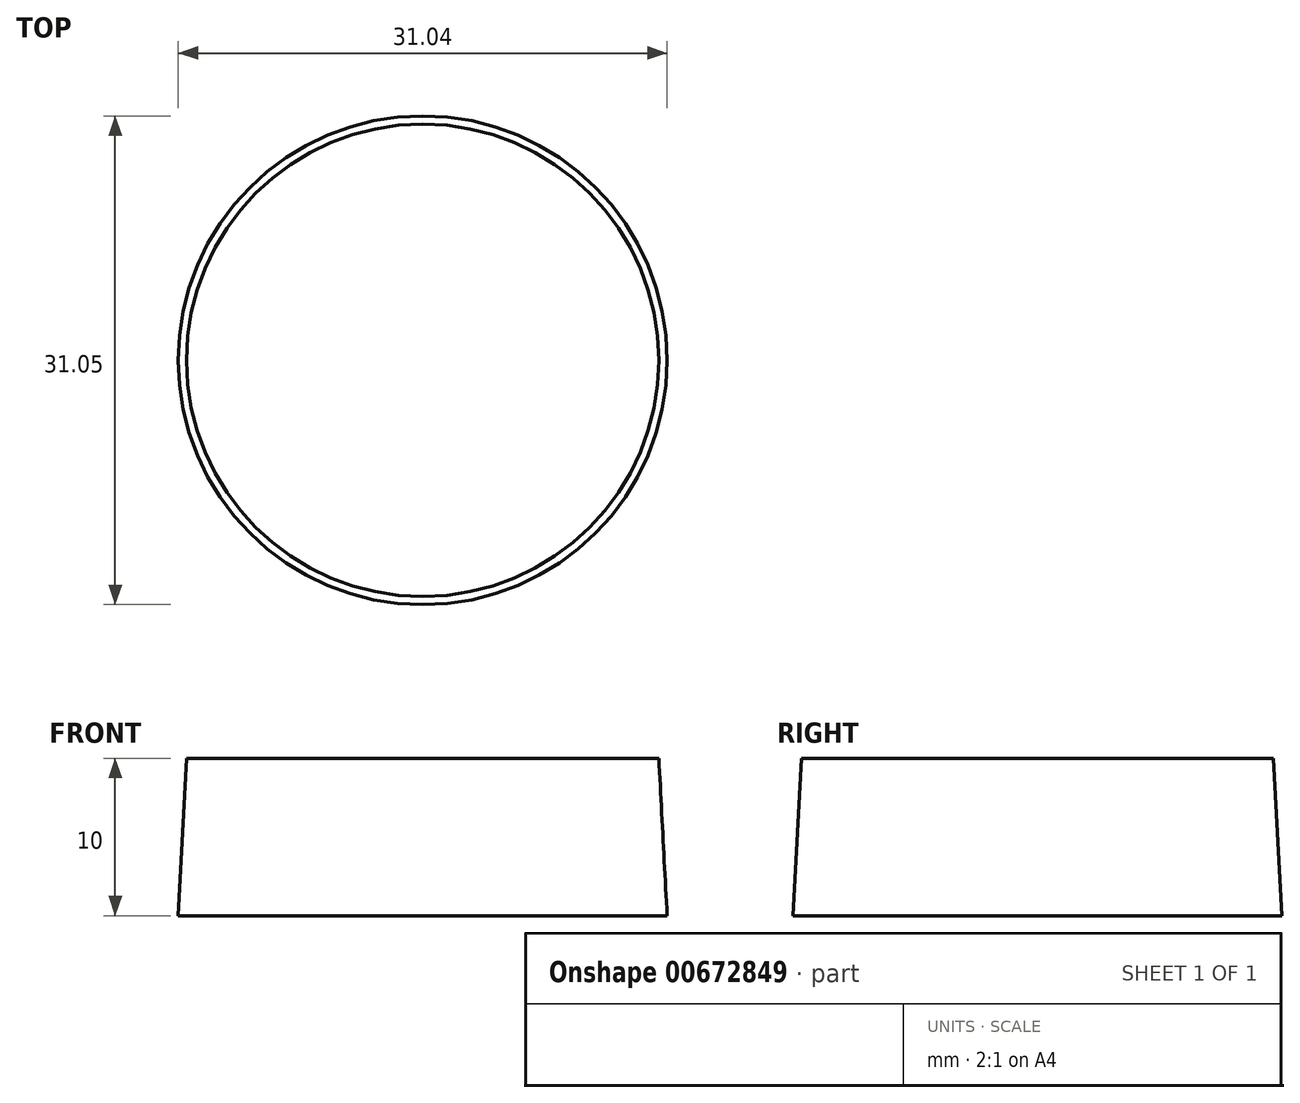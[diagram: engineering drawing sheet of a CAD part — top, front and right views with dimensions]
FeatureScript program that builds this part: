
annotation { "Feature Type Name" : "Feature", "Feature Type Description" : "" }
export const myFeature = defineFeature(function(context is Context, id is Id, definition is map)
    precondition{}
    {
        {
            var Q0;
            Q0=qCreatedBy(makeId("Top.planeOp"),FACE);
            var sketch = newSketch(context, id + "F0", { "sketchPlane" : qUnion([Q0])});
            skCircle(sketch, "E0", {"center": v(0, 12.12) * mm, "radius": 15 * mm});
            skSolve(sketch);
        }
        {
            var Q0;
            Q0=makeQuery(id+"F0.imprint","IMPRINT",FACE,{"disambiguationData":[TD([[makeQuery(id+"F0.imprint","IMPRINT",EDGE,{"derivedFrom":sQuery(id+"F0.wireOp",EDGE,"E0")}),1.0]])]});
            extrude(context, id + "F1", {"entities" : qUnion([Q0]), "oppositeDirection" : true, "depth" : 10 * mm, "offsetDistance" : 25.4 * mm, "hasDraft" : true, "draftAngle" : 3 * degree});
        }
    });
